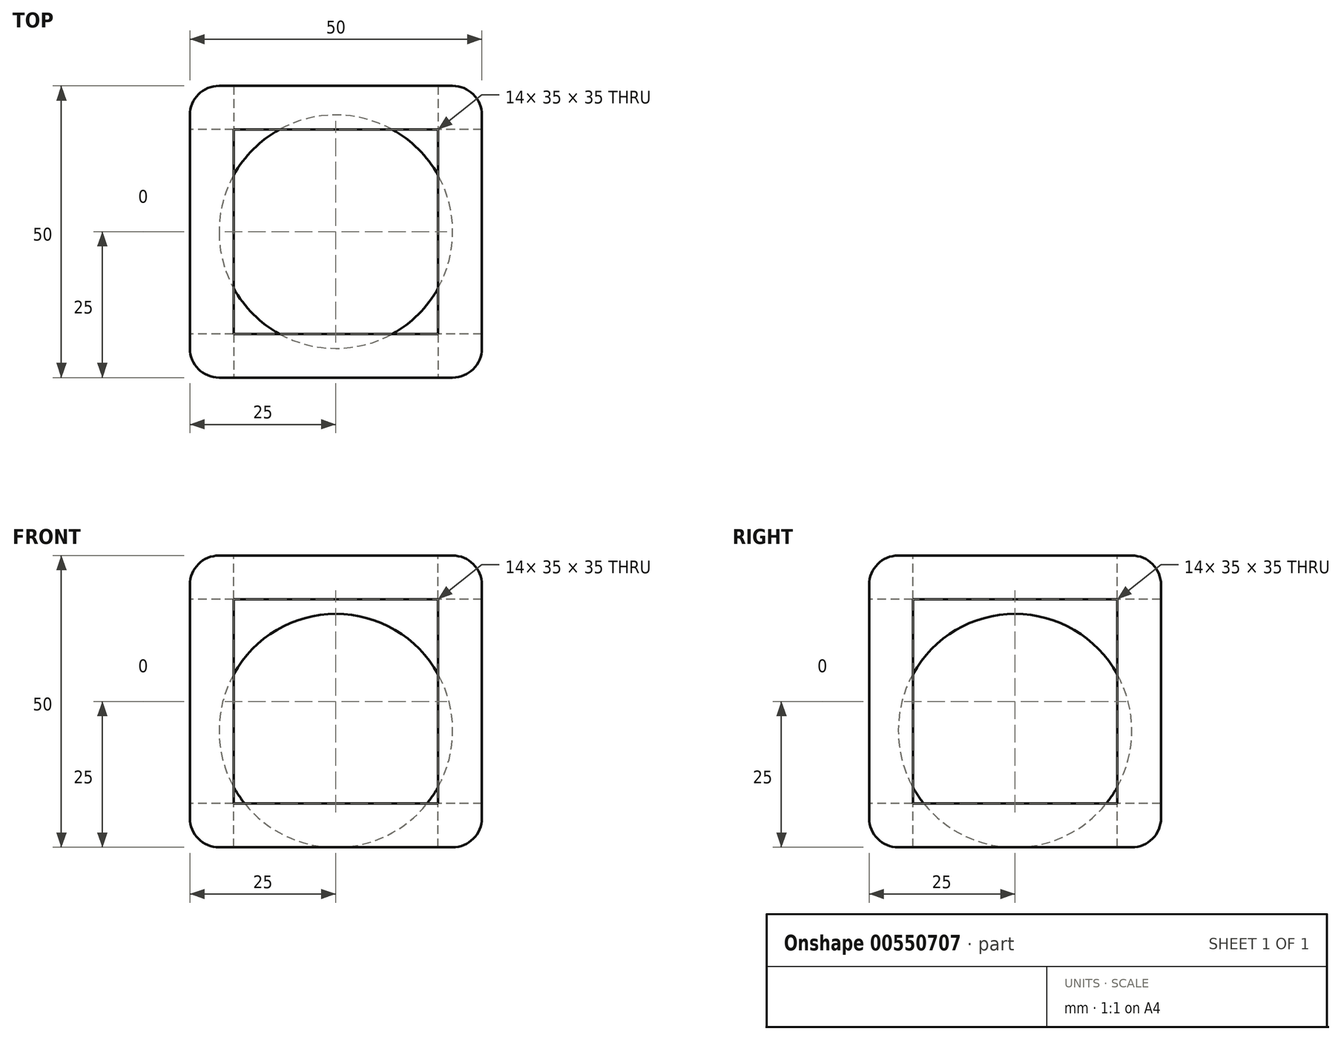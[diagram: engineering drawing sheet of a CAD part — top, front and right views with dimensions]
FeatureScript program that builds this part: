
annotation { "Feature Type Name" : "Feature", "Feature Type Description" : "" }
export const myFeature = defineFeature(function(context is Context, id is Id, definition is map)
    precondition{}
    {
        {
            var Q0;
            Q0=qCreatedBy(makeId("Top.planeOp"),FACE);
            var sketch = newSketch(context, id + "F0", { "sketchPlane" : qUnion([Q0])});
            skLineSegment(sketch, "E0.bottom", {"start": v(25, -25) * mm, "end": v(-25, -25) * mm});
            skLineSegment(sketch, "E0.top", {"start": v(25, 25) * mm, "end": v(-25, 25) * mm});
            skLineSegment(sketch, "E0.left", {"start": v(25, -25) * mm, "end": v(25, 25) * mm});
            skLineSegment(sketch, "E0.right", {"start": v(-25, -25) * mm, "end": v(-25, 25) * mm});
            skPoint(sketch, "E0.middle", {"position": v(0, 0) * mm});
            skSolve(sketch);
        }
        {
            var Q0;
            Q0=makeQuery(id+"F0.imprint","IMPRINT",FACE,{"disambiguationData":[TD([[makeQuery(id+"F0.imprint","IMPRINT",EDGE,{"derivedFrom":sQuery(id+"F0.wireOp",EDGE,"E0.bottom")}),-1.0]])]});
            extrude(context, id + "F1", {"entities" : qUnion([Q0]), "depth" : 50 * mm, "offsetDistance" : 25 * mm});
        }
        {
            var Q0;
            Q0=makeQuery(id+"F1.opExtrude","CAP_EDGE",EDGE,{"disambiguationData":[OSD([sQuery(id+"F0.wireOp",EDGE,"E0.left")])],"isStart":false});
            var Q1;
            Q1=makeQuery(id+"F1.opExtrude","CAP_EDGE",EDGE,{"disambiguationData":[OSD([sQuery(id+"F0.wireOp",EDGE,"E0.bottom")])],"isStart":false});
            var Q2;
            Q2=makeQuery(id+"F1.opExtrude","CAP_EDGE",EDGE,{"disambiguationData":[OSD([sQuery(id+"F0.wireOp",EDGE,"E0.right")])],"isStart":false});
            var Q3;
            Q3=makeQuery(id+"F1.opExtrude","CAP_EDGE",EDGE,{"disambiguationData":[OSD([sQuery(id+"F0.wireOp",EDGE,"E0.top")])],"isStart":false});
            var Q4;
            Q4=makeQuery(id+"F1.opExtrude","SWEPT_EDGE",EDGE,{"disambiguationData":[OSD([sQuery(id+"F0.wireOp",EDGE,"E0.bottom"),sQuery(id+"F0.wireOp",EDGE,"E0.left")])]});
            var Q5;
            Q5=makeQuery(id+"F1.opExtrude","SWEPT_EDGE",EDGE,{"disambiguationData":[OSD([sQuery(id+"F0.wireOp",EDGE,"E0.top"),sQuery(id+"F0.wireOp",EDGE,"E0.left")])]});
            var Q6;
            Q6=makeQuery(id+"F1.opExtrude","SWEPT_EDGE",EDGE,{"disambiguationData":[OSD([sQuery(id+"F0.wireOp",EDGE,"E0.top"),sQuery(id+"F0.wireOp",EDGE,"E0.right")])]});
            var Q7;
            Q7=makeQuery(id+"F1.opExtrude","CAP_EDGE",EDGE,{"disambiguationData":[OSD([sQuery(id+"F0.wireOp",EDGE,"E0.top")])],"isStart":true});
            var Q8;
            Q8=makeQuery(id+"F1.opExtrude","CAP_EDGE",EDGE,{"disambiguationData":[OSD([sQuery(id+"F0.wireOp",EDGE,"E0.right")])],"isStart":true});
            var Q9;
            Q9=makeQuery(id+"F1.opExtrude","SWEPT_EDGE",EDGE,{"disambiguationData":[OSD([sQuery(id+"F0.wireOp",EDGE,"E0.bottom"),sQuery(id+"F0.wireOp",EDGE,"E0.right")])]});
            var Q10;
            Q10=makeQuery(id+"F1.opExtrude","CAP_EDGE",EDGE,{"disambiguationData":[OSD([sQuery(id+"F0.wireOp",EDGE,"E0.bottom")])],"isStart":true});
            var Q11;
            Q11=makeQuery(id+"F1.opExtrude","CAP_EDGE",EDGE,{"disambiguationData":[OSD([sQuery(id+"F0.wireOp",EDGE,"E0.left")])],"isStart":true});
            fillet(context, id + "F2", {"entities" : qUnion([Q0, Q1, Q2, Q3, Q4, Q5, Q6, Q7, Q8, Q9, Q10, Q11]), "radius" : 5 * mm, "tangentPropagation" : true, "allowEdgeOverflow" : false});
        }
        {
            var Q0;
            Q0=makeQuery(id+"F1.opExtrude","CAP_FACE",FACE,{"disambiguationData":[OSD([sQuery(id+"F0.wireOp",EDGE,"E0.bottom"),sQuery(id+"F0.wireOp",EDGE,"E0.top"),sQuery(id+"F0.wireOp",EDGE,"E0.left"),sQuery(id+"F0.wireOp",EDGE,"E0.right")])],"isStart":false});
            var sketch = newSketch(context, id + "F3", { "sketchPlane" : qUnion([Q0])});
            skLineSegment(sketch, "E1.bottom", {"start": v(17.5, -17.5) * mm, "end": v(-17.5, -17.5) * mm});
            skLineSegment(sketch, "E1.top", {"start": v(17.5, 17.5) * mm, "end": v(-17.5, 17.5) * mm});
            skLineSegment(sketch, "E1.left", {"start": v(17.5, -17.5) * mm, "end": v(17.5, 17.5) * mm});
            skLineSegment(sketch, "E1.right", {"start": v(-17.5, -17.5) * mm, "end": v(-17.5, 17.5) * mm});
            skPoint(sketch, "E1.middle", {"position": v(0, 0) * mm});
            skSolve(sketch);
        }
        {
            var Q0;
            Q0=makeQuery(id+"F3.imprint","IMPRINT",FACE,{"disambiguationData":[TD([[makeQuery(id+"F3.imprint","IMPRINT",EDGE,{"derivedFrom":sQuery(id+"F3.wireOp",EDGE,"E1.bottom")}),-1.0]])]});
            extrude(context, id + "F4", {"entities" : qUnion([Q0]), "operationType" : NewBodyOperationType.REMOVE, "oppositeDirection" : true, "depth" : 56.8 * mm, "offsetDistance" : 25 * mm});
        }
        {
            var Q0;
            Q0=makeQuery(id+"F1.opExtrude","SWEPT_FACE",FACE,{"disambiguationData":[OSD([sQuery(id+"F0.wireOp",EDGE,"E0.right")])]});
            var sketch = newSketch(context, id + "F5", { "sketchPlane" : qUnion([Q0])});
            skLineSegment(sketch, "E2.bottom", {"start": v(17.5, 7.5) * mm, "end": v(-17.5, 7.5) * mm});
            skLineSegment(sketch, "E2.top", {"start": v(17.5, 42.5) * mm, "end": v(-17.5, 42.5) * mm});
            skLineSegment(sketch, "E2.left", {"start": v(17.5, 7.5) * mm, "end": v(17.5, 42.5) * mm});
            skLineSegment(sketch, "E2.right", {"start": v(-17.5, 7.5) * mm, "end": v(-17.5, 42.5) * mm});
            skPoint(sketch, "E2.middle", {"position": v(0, 25) * mm});
            skPoint(sketch, "E2.middle.positionSnap0", {"position": v(20, 25) * mm});
            skPoint(sketch, "E2.middle.positionSnap1", {"position": v(0, 45) * mm});
            skPoint(sketch, "E2.centerSnap0", {"position": v(20, 25) * mm});
            skPoint(sketch, "E2.centerSnap1", {"position": v(0, 45) * mm});
            skSolve(sketch);
        }
        {
            var Q0;
            Q0=makeQuery(id+"F5.imprint","IMPRINT",FACE,{"disambiguationData":[TD([[makeQuery(id+"F5.imprint","IMPRINT",EDGE,{"derivedFrom":sQuery(id+"F5.wireOp",EDGE,"E2.bottom")}),-1.0]])]});
            extrude(context, id + "F6", {"entities" : qUnion([Q0]), "operationType" : NewBodyOperationType.REMOVE, "oppositeDirection" : true, "depth" : 65.6 * mm, "offsetDistance" : 25 * mm});
        }
        {
            var Q0;
            Q0=makeQuery(id+"F1.opExtrude","SWEPT_FACE",FACE,{"disambiguationData":[OSD([sQuery(id+"F0.wireOp",EDGE,"E0.bottom")])]});
            var sketch = newSketch(context, id + "F7", { "sketchPlane" : qUnion([Q0])});
            skLineSegment(sketch, "E3.bottom", {"start": v(17.5, 7.5) * mm, "end": v(-17.5, 7.5) * mm});
            skLineSegment(sketch, "E3.top", {"start": v(17.5, 42.5) * mm, "end": v(-17.5, 42.5) * mm});
            skLineSegment(sketch, "E3.left", {"start": v(17.5, 7.5) * mm, "end": v(17.5, 42.5) * mm});
            skLineSegment(sketch, "E3.right", {"start": v(-17.5, 7.5) * mm, "end": v(-17.5, 42.5) * mm});
            skPoint(sketch, "E3.middle", {"position": v(0, 25) * mm});
            skPoint(sketch, "E3.middle.positionSnap0", {"position": v(20, 25) * mm});
            skPoint(sketch, "E3.centerSnap0", {"position": v(20, 25) * mm});
            skSolve(sketch);
        }
        {
            var Q0;
            Q0=makeQuery(id+"F7.imprint","IMPRINT",FACE,{"disambiguationData":[TD([[makeQuery(id+"F7.imprint","IMPRINT",EDGE,{"derivedFrom":sQuery(id+"F7.wireOp",EDGE,"E3.bottom")}),-1.0]])]});
            extrude(context, id + "F8", {"entities" : qUnion([Q0]), "operationType" : NewBodyOperationType.REMOVE, "endBound" : BoundingType.SYMMETRIC, "oppositeDirection" : true, "depth" : 108 * mm, "offsetDistance" : 25 * mm});
        }
        {
            var Q0;
            Q0=qCreatedBy(makeId("Front.planeOp"),FACE);
            var sketch = newSketch(context, id + "F9", { "sketchPlane" : qUnion([Q0])});
            skLineSegment(sketch, "E4", {"start": v(0, 0) * mm, "end": v(0, 20) * mm, "construction": true});
            skCircle(sketch, "E5", {"center": v(0, 20) * mm, "radius": 20 * mm});
            skLineSegment(sketch, "E6", {"start": v(0, 0) * mm, "end": v(0, 40) * mm});
            skSolve(sketch);
        }
        {
            var Q0;
            {var subQ0=sQuery(id+"F9.wireOp",EDGE,"E6");Q0=makeQuery(id+"F9.imprint","IMPRINT",FACE,{"disambiguationData":[TD([[makeQuery(id+"F9.imprint","IMPRINT",EDGE,{"derivedFrom":subQ0}),-1.0]])]});}
            var Q1;
            Q1=sQuery(id+"F9.wireOp",EDGE,"E6");
            revolve(context, id + "F10", {"entities" : qUnion([Q0]), "axis" : qUnion([Q1]), "revolveType" : RevolveType.FULL});
        }
    });
